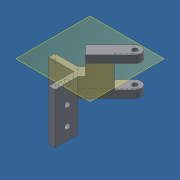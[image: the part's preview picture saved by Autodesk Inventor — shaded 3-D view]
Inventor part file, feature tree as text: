
AUTODESK INVENTOR PART (.ipt)
format: ipt  version: 2021 (Build 250183000, 183)  size: 162,304 bytes
history: native  units: mm
features: extrude x6, sketch x6, other x1, plane x1, projected_geometry x1
ambient origin geometry x8: Origin, YZ Plane, XZ Plane, XY Plane, X Axis, Y Axis, Z Axis, Center Point
bodies: Solid1 (feature_tree)
feature tree (15):
  other  "<userpath>\OneDrive\Objet3D\3DPrinter\Parameters.xlsx"
  extrude  "Extrusion1"  Depth=20.0mm
  plane  "Work Plane1"
  sketch  "Sketch3"  dims[d2=5.0mm d3=5.0mm]
  extrude  "Extrusion3"  Depth=5.0mm
  extrude  "Extrusion5"  Depth=30.0mm
  sketch  "Sketch8"  dims[d8=24.25mm d9=3.7mm]
  extrude  "Extrusion8"  Depth=3.7mm
  extrude  "Extrusion9"  Depth=25.0mm
  extrude  "Extrusion10"  Depth=5.0mm
  sketch  "Sketch1"  dims[d0=20.0mm d1=20.0mm]
  sketch  "Sketch5"  dims[d5=30.0mm d6=0.0mm d7=24.25mm]
  projected_geometry  "Projected Loop2"
  sketch  "Sketch9"  dims[d10=-6.0mm d13=25.0mm]
  sketch  "Sketch10"  dims[d16=18.0mm d17=0.0mm d18=5.0mm d19=135.0deg d22=25.0mm d23=0.0mm d40=4.5mm d41=10.0mm d42=10.0mm d43=4.5mm d44=10.0mm d45=15.0mm d46=10.0mm d47=10.0mm d48=10.0mm d49=15.0mm d50=4.5mm d51=4.5mm d52=20.0mm d53=0.0mm d54=20.0mm d55=0.0mm d56=135.0deg d57=0.0mm d58=15.0mm d59=0.0mm]
